# Revit family: Storage_Top-Teknion-CCCT_Credenza_Top-R2022
name_source: partatom
category: Furniture
units: mm (PartAtom-declared; Revit-internal decimal feet)

## family parameters
Always vertical = Yes
Cut with Voids When Loaded = No
OmniClass Number = 23.40.20.00
OmniClass Title = General Furniture and Specialties
Render Appearance Source = Family Geometry
Room Calculation Point = No
Shared = Yes
Work Plane-Based = No

## types (2) — shared parameters
Assembly Code = E2020200
Manufacturer = Teknion
Manufacturer Fax = 416.661.4586
Part Number = CCCT
Product Line = Chronicle
Series = Chronicle
Sustainability Data = https://www.teknion.com
URL = www.teknion.com
Unit Weight URL = http://www.teknion.com
Warranty = http://www.teknion.com
zero-valued in all types: Default Elevation

## per-type parameters (varying)
| type | Depth | Description | Model | Product Documentation Link | Product Page URL |
| 20" Depth | 20 " | Credenza Top 20" Depth | CCCT20 |  |  |
| 24" Depth | 24 " | Credenza Top 24"Depth | CCCT24 | https://www.teknion.com | https://www.teknion.com |

## geometry (parser evidence)
native form markers: Sweep x3
no freeform markers — native parametric forms only
